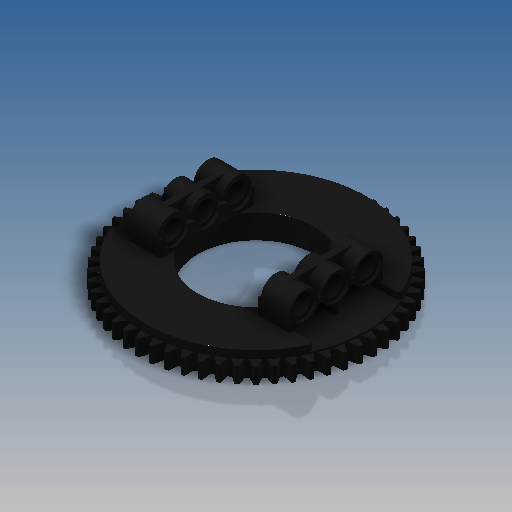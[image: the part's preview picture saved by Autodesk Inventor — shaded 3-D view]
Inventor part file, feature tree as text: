
AUTODESK INVENTOR PART (.ipt)
format: ipt  version: 2018.3 (Build 223284000, 284)  size: 1,615,872 bytes
history: native  units: in
note: dims shown in document units (in); Inventor stores cm internally (conversion verified against a paired STEP export)
features: extrude x8, sketch x7, fillet x2, plane x2, revolve x1, pattern_circular x1, mirror x1
ambient origin geometry x8: Origin, YZ Plane, XZ Plane, XY Plane, X Axis, Y Axis, Z Axis, Center Point
bodies: Solid1 (feature_tree)
feature tree (22):
  revolve  "Revolution1"  [1 undecoded]
  extrude  "Extrusion10"  Depth=0.5512in
  extrude  "Extrusion11"  Depth=0.252in
  fillet  "Fillet2"  Radius=0.189in
  pattern_circular  "Circular Pattern3"  [2 undecoded]
  extrude  "Extrusion12"  Depth=0.0039in
  plane  "Work Plane1"
  sketch  "Sketch4"  dims[d37=0.2835in d39=0.252in d40=0.189in]
  extrude  "Extrusion4"  Depth=0.0039in
  extrude  "Extrusion13"  Depth=0.0315in TaperAngle=0.0deg
  extrude  "Extrusion6"  Depth=0.0315in
  plane  "Work Plane2"
  extrude  "Extrusion7"  TaperAngle=0.0deg  [1 undecoded]
  extrude  "Extrusion8"  Depth=0.0039in
  mirror  "Mirror1"
  fillet  "Fillet1"  Radius=1.1339in
  sketch  "Sketch2"  dims[d1=2.1575in d4=0.063in]
  sketch  "Sketch3"  dims[d6=90.0deg d31=0.5512in d32=-0.7874in]
  sketch  "Sketch5"  dims[d41=0.315in]
  sketch  "Sketch6"  dims[d42=0.0543in]
  sketch  "Sketch8"  dims[d44=0.2835in d45=0.0in]
  sketch  "Sketch9"  dims[d49=0.252in d50=0.0315in d51=0.0866in d52=0.0in d53=0.0in d54=0.0787in d55=0.063in d56=0.0315in d57=0.0in d58=0.0315in d59=0.0in d66=0.0039in d67=1.1339in d68=0.2362in d69=1.2598in d72=2.0157in d73=0.9449in d74=0.063in d75=0.0in d76=0.0907in d78=0.0328in d79=0.0874in d80=0.1575in d81=0.0in d82=22.0472in d83=360.0deg d85=1.2598in d86=0.8303in d87=0.063in d88=0.0in d89=0.1575in d90=0.0472in d91=0.2835in d92=0.063in d93=0.0in d94=0.0315in d95=0.0039in]
note: 4 required parameter values undecoded (feature->parameter linkage not recoverable at this tier; creation-order binding heuristic only, values carry confidence <= 0.55)